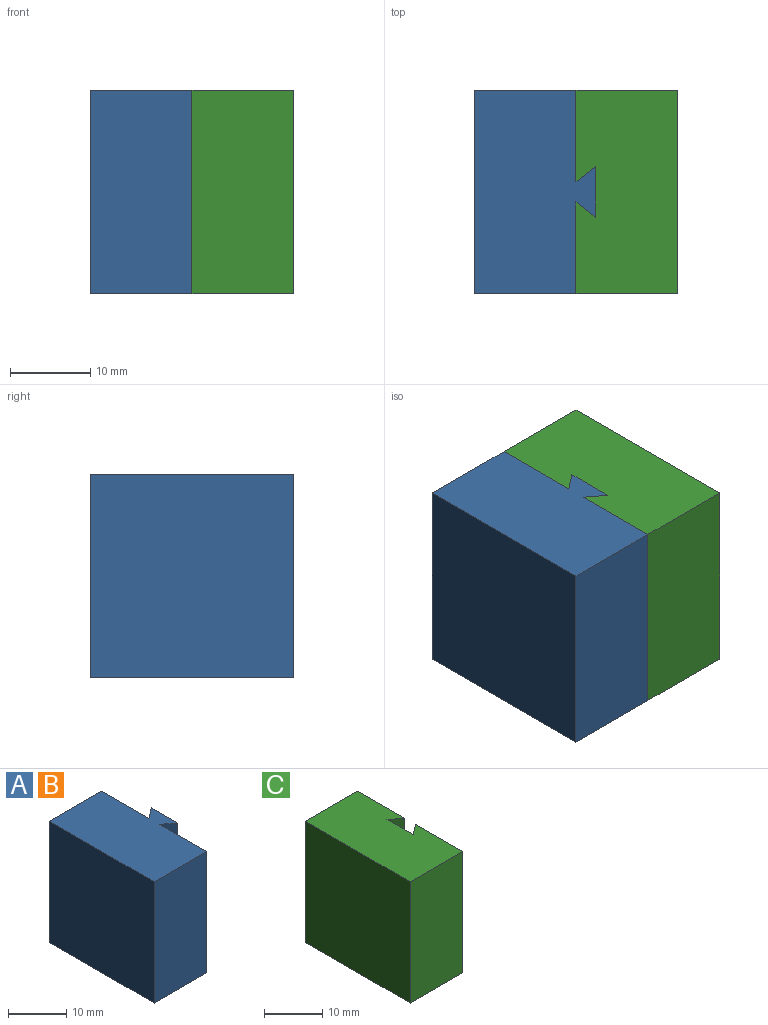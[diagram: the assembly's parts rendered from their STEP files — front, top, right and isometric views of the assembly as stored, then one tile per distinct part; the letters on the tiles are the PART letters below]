
ASSEMBLY  parts=3 mates=1
PART A: 10 faces, bbox 15.1x25.4x25.4 mm
  f0: plane 25.4x11.43mm, normal (1,0,0), area 290.3mm2, adj f4,f5,f6,f7
  f1: plane 25.4x25.4mm, normal (-1,0,0), area 645.2mm2, adj f2,f4,f5,f6
  f2: plane 25.4x12.7mm, normal (0,-1,0), area 322.6mm2, adj f1,f3,f5,f6
  f3: plane 25.4x11.43mm, normal (1,0,0), area 290.3mm2, adj f2,f5,f6,f8
  f4: plane 25.4x12.7mm, normal (0,1,0), area 322.6mm2, adj f0,f1,f5,f6
  f5: plane 25.4x15.15mm, normal (0,0,1), area 333.5mm2, adj f0,f1,f2,f3,f4,f7,f8,f9
  f6: plane 25.4x15.15mm, normal (0,0,-1), area 333.5mm2, adj f0,f1,f2,f3,f4,f7,f8,f9
  f7: plane 25.4x2.45mm, normal (-0.61,0.79,0), area 78.8mm2, adj f0,f5,f6,f9
  f8: plane 25.4x2.45mm, normal (-0.61,-0.79,0), area 78.8mm2, adj f3,f5,f6,f9
  f9: plane 25.4x6.35mm, normal (1,0,0), area 161.3mm2, adj f5,f6,f7,f8
PART B: same geometry as A
PART C: 10 faces, bbox 12.7x25.4x25.4 mm
  f0: plane 25.4x11.43mm, normal (1,0,0), area 290.3mm2, adj f4,f5,f6,f7
  f1: plane 25.4x25.4mm, normal (-1,0,0), area 645.2mm2, adj f2,f4,f5,f6
  f2: plane 25.4x12.7mm, normal (0,-1,0), area 322.6mm2, adj f1,f3,f5,f6
  f3: plane 25.4x11.43mm, normal (1,0,0), area 290.3mm2, adj f2,f5,f6,f9
  f4: plane 25.4x12.7mm, normal (0,1,0), area 322.6mm2, adj f0,f1,f5,f6
  f5: plane 25.4x12.7mm, normal (0,0,1), area 311.7mm2, adj f0,f1,f2,f3,f4,f7,f8,f9
  f6: plane 25.4x12.7mm, normal (0,0,-1), area 311.7mm2, adj f0,f1,f2,f3,f4,f7,f8,f9
  f7: plane 25.4x2.45mm, normal (-0.61,-0.79,0), area 78.8mm2, adj f0,f5,f6,f8
  f8: plane 25.4x6.35mm, normal (1,0,0), area 161.3mm2, adj f5,f6,f7,f9
  f9: plane 25.4x2.45mm, normal (-0.61,0.79,0), area 78.8mm2, adj f3,f5,f6,f8
PLACE A t=(0.14,0.18,-0.05)mm
PLACE B t=(0.14,0.18,-0.05)mm fixed
PLACE C rot(axis=(0,0,-1),180deg) t=(25.54,25.58,-0.05)mm
MATE fastened B.f9 <-> C.f8  axis (1,0,0) through (15.29,12.88,12.65)mm
